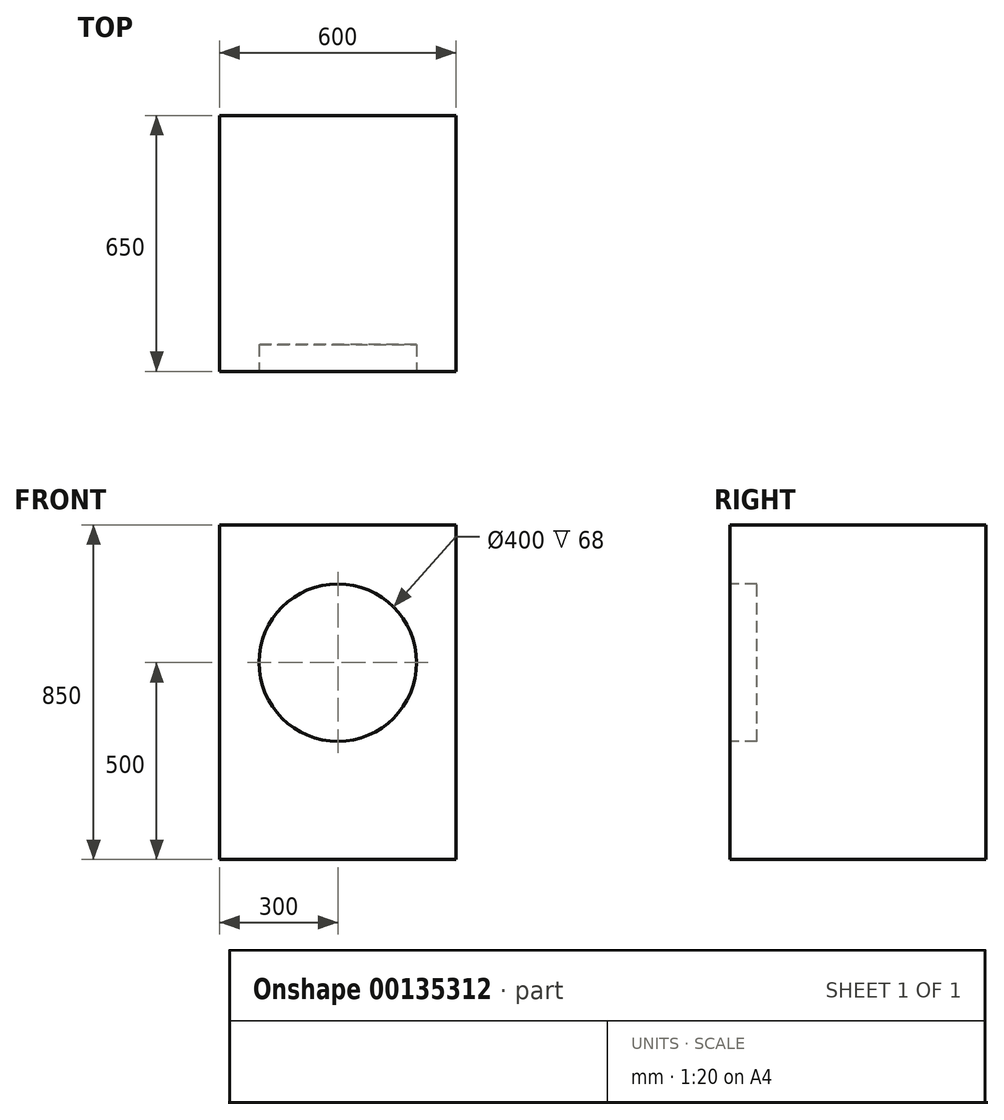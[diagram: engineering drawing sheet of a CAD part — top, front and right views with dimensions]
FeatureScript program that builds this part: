
annotation { "Feature Type Name" : "Feature", "Feature Type Description" : "" }
export const myFeature = defineFeature(function(context is Context, id is Id, definition is map)
    precondition{}
    {
        {
            var Q0;
            Q0=qCreatedBy(makeId("Top.planeOp"),FACE);
            var sketch = newSketch(context, id + "F0", { "sketchPlane" : qUnion([Q0])});
            skLineSegment(sketch, "E0.bottom", {"start": v(300, 325) * mm, "end": v(-300, 325) * mm});
            skLineSegment(sketch, "E0.top", {"start": v(300, -325) * mm, "end": v(-300, -325) * mm});
            skLineSegment(sketch, "E0.left", {"start": v(300, 325) * mm, "end": v(300, -325) * mm});
            skLineSegment(sketch, "E0.right", {"start": v(-300, 325) * mm, "end": v(-300, -325) * mm});
            skPoint(sketch, "E0.middle", {"position": v(0, 0) * mm});
            skSolve(sketch);
        }
        {
            var Q0;
            Q0 = qSketchRegion(id + "F0", true);
            extrude(context, id + "F1", {"entities" : qUnion([Q0]), "depth" : 850 * mm});
        }
        {
            var Q0;
            Q0=makeQuery(id+"F1.opExtrude","SWEPT_FACE",FACE,{"disambiguationData":[OSD([sQuery(id+"F0.wireOp",EDGE,"E0.top")])]});
            var sketch = newSketch(context, id + "F2", { "sketchPlane" : qUnion([Q0])});
            skCircle(sketch, "E1", {"center": v(0, 500) * mm, "radius": 200 * mm});
            skSolve(sketch);
        }
        {
            var Q0;
            Q0 = qSketchRegion(id + "F2", true);
            extrude(context, id + "F3", {"entities" : qUnion([Q0]), "operationType" : NewBodyOperationType.REMOVE, "oppositeDirection" : true, "depth" : 68 * mm});
        }
    });
